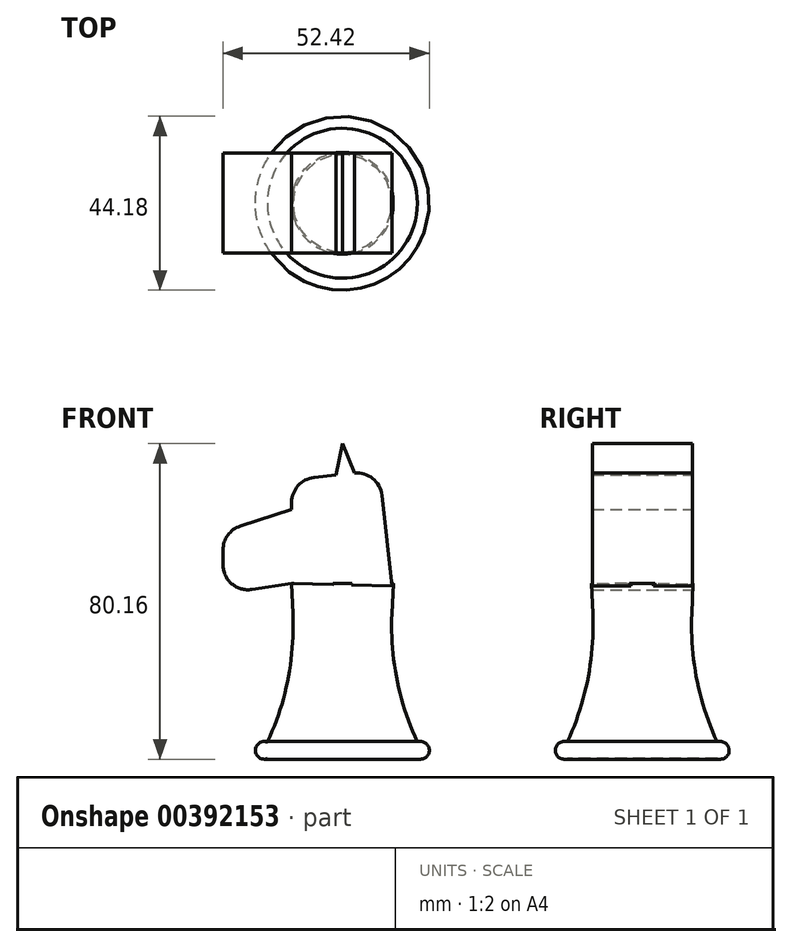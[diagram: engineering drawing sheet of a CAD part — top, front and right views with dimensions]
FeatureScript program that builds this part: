
annotation { "Feature Type Name" : "Feature", "Feature Type Description" : "" }
export const myFeature = defineFeature(function(context is Context, id is Id, definition is map)
    precondition{}
    {
        {
            var Q0;
            Q0=qCreatedBy(makeId("Front.planeOp"),FACE);
            var sketch = newSketch(context, id + "F0", { "sketchPlane" : qUnion([Q0])});
            skLineSegment(sketch, "E0", {"start": v(0, -50.97) * mm, "end": v(0, 6.18) * mm});
            skLineSegment(sketch, "E1", {"start": v(0, -50.97) * mm, "end": v(-19.05, -50.97) * mm});
            skArc(sketch, "E2", {"start": v(-19.05, -46.78) * mm, "mid": v(-22.09, -48.88) * mm, "end": v(-19.05, -50.97) * mm});
            skArc(sketch, "E3", {"start": v(-19.05, -46.78) * mm, "mid": v(-13.85, -30.88) * mm, "end": v(-12.58, -14.2) * mm});
            skLineSegment(sketch, "E4", {"start": v(-12.58, -14.2) * mm, "end": v(-12.92, -6.47) * mm});
            skLineSegment(sketch, "E5", {"start": v(-12.92, -6.47) * mm, "end": v(0, -6.47) * mm});
            skSolve(sketch);
        }
        {
            var Q0;
            Q0=qSketchRegion(id+"F0",true);
            var Q1;
            Q1=sQuery(id+"F0.wireOp",EDGE,"E0");
            revolve(context, id + "F1", {"entities" : qUnion([Q0]), "axis" : qUnion([Q1]), "revolveType" : RevolveType.FULL});
        }
        {
            var Q0;
            Q0=qCreatedBy(makeId("Front.planeOp"),FACE);
            var sketch = newSketch(context, id + "F2", { "sketchPlane" : qUnion([Q0])});
            skLineSegment(sketch, "E6", {"start": v(12.58, -7.1) * mm, "end": v(10.05, 15.95) * mm});
            skLineSegment(sketch, "E7", {"start": v(3.04, 21.57) * mm, "end": v(-7.23, 20.44) * mm});
            skLineSegment(sketch, "E8", {"start": v(-12.88, 14.13) * mm, "end": v(-12.88, -6.45) * mm});
            skLineSegment(sketch, "E9", {"start": v(-12.88, -6.45) * mm, "end": v(12.58, -7.1) * mm});
            skLineSegment(sketch, "E10", {"start": v(-12.88, 12.3) * mm, "end": v(-25.93, 8.1) * mm});
            skPoint(sketch, "E10.endSnap0", {"position": v(-12.88, 6.68) * mm});
            skLineSegment(sketch, "E11", {"start": v(-12.88, -6.45) * mm, "end": v(-23.01, -8) * mm});
            skLineSegment(sketch, "E12", {"start": v(-30.33, -1.73) * mm, "end": v(-30.33, 2.06) * mm});
            skPoint(sketch, "E13.visualSharp", {"position": v(9.36, 22.26) * mm});
            skArc(sketch, "E13.filletArc", {"start": v(10.05, 15.95) * mm, "mid": v(7.71, 20.2) * mm, "end": v(3.04, 21.57) * mm});
            skPoint(sketch, "E14.visualSharp", {"position": v(-12.88, 19.82) * mm});
            skArc(sketch, "E14.filletArc", {"start": v(-7.23, 20.44) * mm, "mid": v(-11.26, 18.36) * mm, "end": v(-12.88, 14.13) * mm});
            skPoint(sketch, "E15.visualSharp", {"position": v(-30.33, 6.68) * mm});
            skArc(sketch, "E15.filletArc", {"start": v(-25.93, 8.1) * mm, "mid": v(-29.1, 5.8) * mm, "end": v(-30.33, 2.06) * mm});
            skPoint(sketch, "E16.visualSharp", {"position": v(-30.33, -9.13) * mm});
            skArc(sketch, "E16.filletArc", {"start": v(-30.33, -1.73) * mm, "mid": v(-28.11, -6.55) * mm, "end": v(-23.01, -8) * mm});
            skLineSegment(sketch, "E17", {"start": v(3.04, 21.57) * mm, "end": v(0, 29.04) * mm});
            skLineSegment(sketch, "E18", {"start": v(0, 29.04) * mm, "end": v(-1.58, 21.06) * mm});
            skSolve(sketch);
        }
        {
            var Q0;
            Q0=qSketchRegion(id+"F2",true);
            extrude(context, id + "F3", {"entities" : qUnion([Q0]), "operationType" : NewBodyOperationType.ADD, "depth" : 12.7 * mm});
        }
        {
            var Q0;
            Q0=qSketchRegion(id+"F2",true);
            extrude(context, id + "F4", {"entities" : qUnion([Q0]), "operationType" : NewBodyOperationType.ADD, "oppositeDirection" : true, "depth" : 12.7 * mm});
        }
    });
